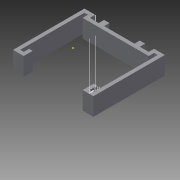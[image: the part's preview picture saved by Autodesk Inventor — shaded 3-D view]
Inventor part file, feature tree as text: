
AUTODESK INVENTOR PART (.ipt)
format: ipt  version: 2015 (Build 190159000, 159)  size: 140,288 bytes
history: native  units: mm
features: sketch x3, extrude x2
ambient origin geometry x8: Origin, YZ Plane, XZ Plane, XY Plane, X Axis, Y Axis, Z Axis, Center Point
bodies: Solid1 (feature_tree)
feature tree (5):
  extrude  "Extrusion1"  Depth=2.0mm
  sketch  "Sketch2"  dims[d2=2.0mm d3=2.0mm]
  extrude  "Extrusion2"  Depth=2.0mm
  sketch  "Sketch1"  dims[d0=40.0mm d1=2.0mm]
  sketch  "Sketch3"  dims[d4=2.0mm d5=5.0mm d6=5.0mm d7=37.0mm d8=6.0mm d9=6.0mm d10=2.0mm d11=2.0mm d12=2.0mm d13=2.0mm d14=2.0mm d15=40.0mm d16=6.0mm d17=6.0mm d18=45.0mm d19=10.0mm d20=0.0mm d21=3.0mm d22=5.0mm d23=5.0mm d24=3.0mm d25=3.0mm d26=3.0mm d27=0.0mm]
